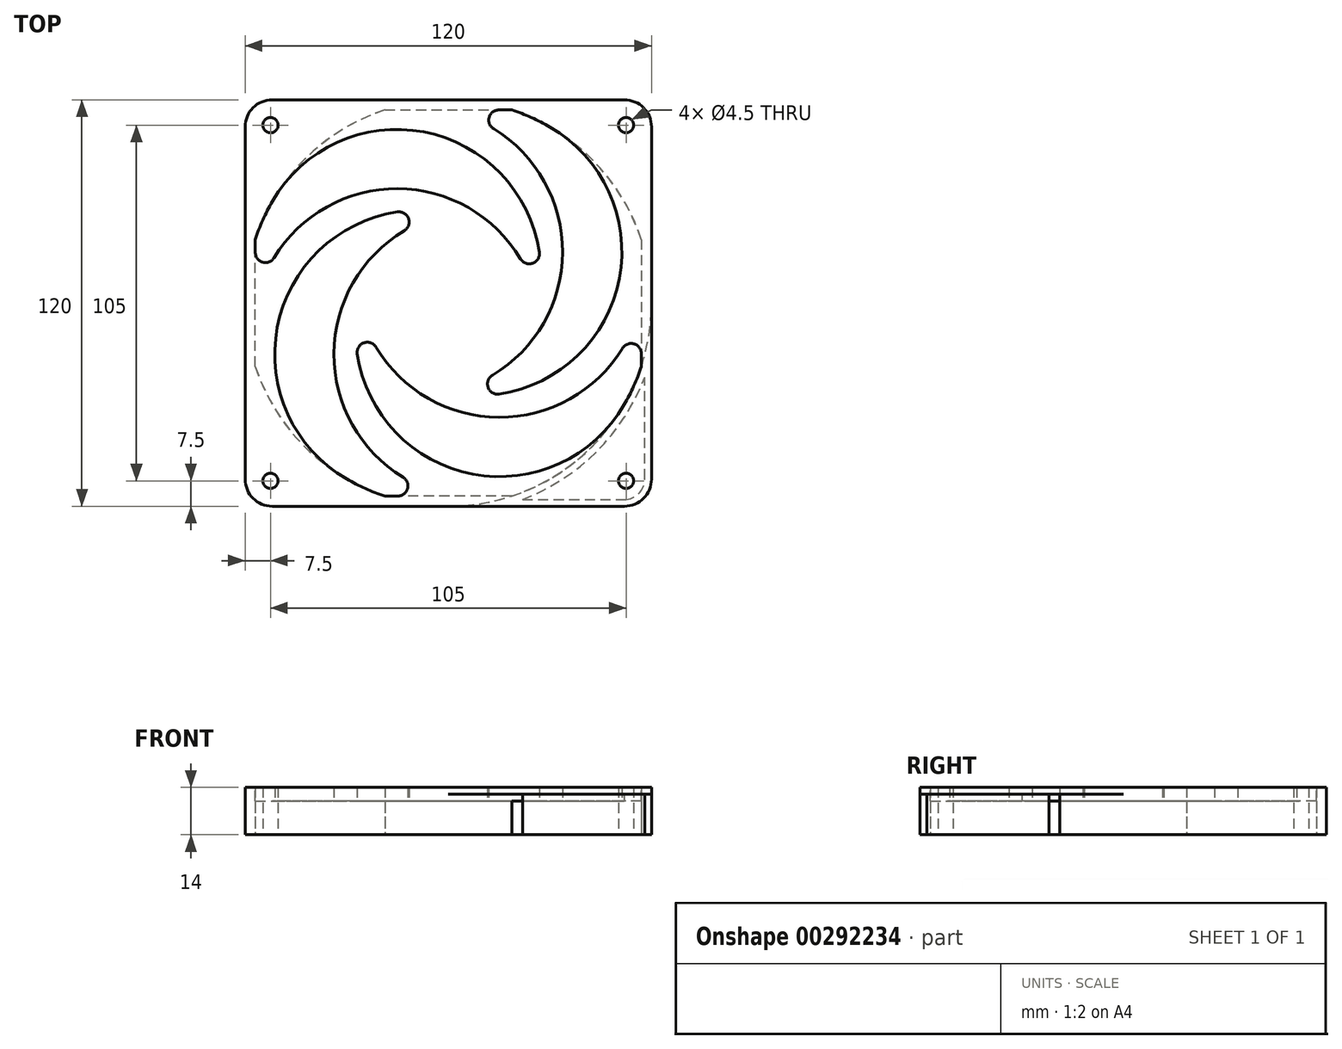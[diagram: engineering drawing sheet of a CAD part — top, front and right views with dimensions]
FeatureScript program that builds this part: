
annotation { "Feature Type Name" : "Feature", "Feature Type Description" : "" }
export const myFeature = defineFeature(function(context is Context, id is Id, definition is map)
    precondition{}
    {
        {
            var Q0;
            Q0=qCreatedBy(makeId("Top.planeOp"),FACE);
            var sketch = newSketch(context, id + "F0", { "sketchPlane" : qUnion([Q0])});
            skCircle(sketch, "E0", {"center": v(0, 0) * mm, "radius": 25 * mm});
            skLineSegment(sketch, "E1.bottom", {"start": v(52, 60) * mm, "end": v(-52, 60) * mm});
            skLineSegment(sketch, "E1.top", {"start": v(52, -60) * mm, "end": v(-52, -60) * mm});
            skLineSegment(sketch, "E1.left", {"start": v(60, 52) * mm, "end": v(60, -52) * mm});
            skLineSegment(sketch, "E1.right", {"start": v(-60, 52) * mm, "end": v(-60, -52) * mm});
            skCircle(sketch, "E2", {"center": v(0, 0) * mm, "radius": 60 * mm});
            skLineSegment(sketch, "E3.bottom", {"start": v(52.5, 52.5) * mm, "end": v(-52.5, 52.5) * mm, "construction": true});
            skLineSegment(sketch, "E3.top", {"start": v(52.5, -52.5) * mm, "end": v(-52.5, -52.5) * mm, "construction": true});
            skLineSegment(sketch, "E3.left", {"start": v(52.5, 52.5) * mm, "end": v(52.5, -52.5) * mm, "construction": true});
            skLineSegment(sketch, "E3.right", {"start": v(-52.5, 52.5) * mm, "end": v(-52.5, -52.5) * mm, "construction": true});
            skCircle(sketch, "E4", {"center": v(-52.5, 52.5) * mm, "radius": 2.25 * mm});
            skCircle(sketch, "E5", {"center": v(52.5, 52.5) * mm, "radius": 2.25 * mm});
            skCircle(sketch, "E6", {"center": v(52.5, -52.5) * mm, "radius": 2.25 * mm});
            skCircle(sketch, "E7", {"center": v(-52.5, -52.5) * mm, "radius": 2.25 * mm});
            skPoint(sketch, "E8.visualSharp", {"position": v(-60, 60) * mm});
            skArc(sketch, "E8.filletArc", {"start": v(-52, 60) * mm, "mid": v(-57.66, 57.66) * mm, "end": v(-60, 52) * mm});
            skPoint(sketch, "E9.visualSharp", {"position": v(60, 60) * mm});
            skArc(sketch, "E9.filletArc", {"start": v(60, 52) * mm, "mid": v(57.66, 57.66) * mm, "end": v(52, 60) * mm});
            skPoint(sketch, "E10.visualSharp", {"position": v(60, -60) * mm});
            skArc(sketch, "E10.filletArc", {"start": v(52, -60) * mm, "mid": v(57.66, -57.66) * mm, "end": v(60, -52) * mm});
            skPoint(sketch, "E11.visualSharp", {"position": v(-60, -60) * mm});
            skArc(sketch, "E11.filletArc", {"start": v(-60, -52) * mm, "mid": v(-57.66, -57.66) * mm, "end": v(-52, -60) * mm});
            skLineSegment(sketch, "E12", {"start": v(-18.73, 57) * mm, "end": v(18.73, 57) * mm});
            skLineSegment(sketch, "E13.1.0", {"start": v(-57, -18.73) * mm, "end": v(-57, 18.73) * mm});
            skLineSegment(sketch, "E13.2.0", {"start": v(18.73, -57) * mm, "end": v(-18.73, -57) * mm});
            skLineSegment(sketch, "E14.1.3.0", {"start": v(57, 18.73) * mm, "end": v(57, -18.73) * mm});
            skSolve(sketch);
        }
        {
            var Q0;
            Q0=makeQuery(id+"F0.imprint","IMPRINT",FACE,{"disambiguationData":[TD([[makeQuery(id+"F0.imprint","IMPRINT",EDGE,{"derivedFrom":sQuery(id+"F0.wireOp",EDGE,"E0")}),1.0]])]});
            var Q1;
            Q1=makeQuery(id+"F0.imprint","IMPRINT",FACE,{"disambiguationData":[TD([[makeQuery(id+"F0.imprint","IMPRINT",EDGE,{"derivedFrom":sQuery(id+"F0.wireOp",EDGE,"E0")}),-1.0]])]});
            var Q2;
            Q2=makeQuery(id+"F0.imprint","IMPRINT",FACE,{"disambiguationData":[TD([[makeQuery(id+"F0.imprint","IMPRINT",EDGE,{"derivedFrom":sQuery(id+"F0.wireOp",EDGE,"E4")}),-1.0]])]});
            var Q3;
            Q3=makeQuery(id+"F0.imprint","IMPRINT",FACE,{"disambiguationData":[TD([[makeQuery(id+"F0.imprint","IMPRINT",EDGE,{"derivedFrom":sQuery(id+"F0.wireOp",EDGE,"E7")}),-1.0]])]});
            var Q4;
            Q4=makeQuery(id+"F0.imprint","IMPRINT",FACE,{"disambiguationData":[TD([[makeQuery(id+"F0.imprint","IMPRINT",EDGE,{"derivedFrom":sQuery(id+"F0.wireOp",EDGE,"E6")}),-1.0]])]});
            var Q5;
            Q5=makeQuery(id+"F0.imprint","IMPRINT",FACE,{"disambiguationData":[TD([[makeQuery(id+"F0.imprint","IMPRINT",EDGE,{"derivedFrom":sQuery(id+"F0.wireOp",EDGE,"E5")}),-1.0]])]});
            var Q6;
            {var subQ0=sQuery(id+"F0.wireOp",EDGE,"E12");Q6=makeQuery(id+"F0.imprint","IMPRINT",FACE,{"disambiguationData":[TD([[makeQuery(id+"F0.imprint","IMPRINT",EDGE,{"derivedFrom":subQ0}),1.0]])]});}
            var Q7;
            {var subQ0=sQuery(id+"F0.wireOp",EDGE,"E13.1.0");Q7=makeQuery(id+"F0.imprint","IMPRINT",FACE,{"disambiguationData":[TD([[makeQuery(id+"F0.imprint","IMPRINT",EDGE,{"derivedFrom":subQ0}),1.0]])]});}
            var Q8;
            {var subQ0=sQuery(id+"F0.wireOp",EDGE,"E13.2.0");Q8=makeQuery(id+"F0.imprint","IMPRINT",FACE,{"disambiguationData":[TD([[makeQuery(id+"F0.imprint","IMPRINT",EDGE,{"derivedFrom":subQ0}),1.0]])]});}
            var Q9;
            {var subQ0=sQuery(id+"F0.wireOp",EDGE,"E14.1.3.0");Q9=makeQuery(id+"F0.imprint","IMPRINT",FACE,{"disambiguationData":[TD([[makeQuery(id+"F0.imprint","IMPRINT",EDGE,{"derivedFrom":subQ0}),1.0]])]});}
            extrude(context, id + "F1", {"entities" : qUnion([Q0, Q1, Q2, Q3, Q4, Q5, Q6, Q7, Q8, Q9]), "depth" : 14 * mm});
        }
        {
            var Q0;
            Q0=makeQuery(id+"F0.imprint","IMPRINT",FACE,{"disambiguationData":[TD([[makeQuery(id+"F0.imprint","IMPRINT",EDGE,{"derivedFrom":sQuery(id+"F0.wireOp",EDGE,"E0")}),-1.0]])]});
            var Q1;
            Q1=makeQuery(id+"F0.imprint","IMPRINT",FACE,{"disambiguationData":[TD([[makeQuery(id+"F0.imprint","IMPRINT",EDGE,{"derivedFrom":sQuery(id+"F0.wireOp",EDGE,"E0")}),1.0]])]});
            extrude(context, id + "F2", {"entities" : qUnion([Q0, Q1]), "operationType" : NewBodyOperationType.REMOVE, "depth" : 10 * mm});
        }
        {
            var Q0;
            Q0=makeQuery(id+"F0.imprint","IMPRINT",FACE,{"disambiguationData":[TD([[makeQuery(id+"F0.imprint","IMPRINT",EDGE,{"derivedFrom":sQuery(id+"F0.wireOp",EDGE,"E0")}),-1.0]])]});
            var sketch = newSketch(context, id + "F3", { "sketchPlane" : qUnion([Q0])});
            skLineSegment(sketch, "E15.0.0", {"start": v(57, -18.73) * mm, "end": v(57, 18.73) * mm});
            skArc(sketch, "E15.0.1", {"start": v(57, 18.73) * mm, "mid": v(42.43, 42.43) * mm, "end": v(18.73, 57) * mm});
            skLineSegment(sketch, "E15.0.2", {"start": v(18.73, 57) * mm, "end": v(-18.73, 57) * mm});
            skArc(sketch, "E15.0.3", {"start": v(-18.73, 57) * mm, "mid": v(-42.43, 42.43) * mm, "end": v(-57, 18.73) * mm});
            skLineSegment(sketch, "E15.0.4", {"start": v(-57, 18.73) * mm, "end": v(-57, -18.73) * mm});
            skArc(sketch, "E15.0.5", {"start": v(-57, -18.73) * mm, "mid": v(-42.43, -42.43) * mm, "end": v(-18.73, -57) * mm});
            skLineSegment(sketch, "E15.0.6", {"start": v(-18.73, -57) * mm, "end": v(18.73, -57) * mm});
            skArc(sketch, "E15.0.7", {"start": v(18.73, -57) * mm, "mid": v(42.43, -42.43) * mm, "end": v(57, -18.73) * mm});
            skCircle(sketch, "E16", {"center": v(0, 0) * mm, "radius": 25 * mm});
            skArc(sketch, "E17", {"start": v(12.5, 21.65) * mm, "mid": v(-45.56, 6.1) * mm, "end": v(-30, -51.96) * mm});
            skLineSegment(sketch, "E18", {"start": v(0, 0) * mm, "end": v(0, -16.93) * mm, "construction": true});
            skLineSegment(sketch, "E19", {"start": v(0, 0) * mm, "end": v(-8.75, -15.16) * mm, "construction": true});
            skArc(sketch, "E20", {"start": v(21.65, 12.5) * mm, "mid": v(-22.5, 33.1) * mm, "end": v(-57, -1.31) * mm});
            skLineSegment(sketch, "E21", {"start": v(0, 0) * mm, "end": v(-15.16, -8.75) * mm, "construction": true});
            skArc(sketch, "E22.1.0", {"start": v(-21.65, 12.5) * mm, "mid": v(-6.1, -45.56) * mm, "end": v(51.96, -30) * mm});
            skArc(sketch, "E22.1.1", {"start": v(-12.5, 21.65) * mm, "mid": v(-33.1, -22.5) * mm, "end": v(1.31, -57) * mm});
            skArc(sketch, "E22.2.0", {"start": v(-12.5, -21.65) * mm, "mid": v(45.56, -6.1) * mm, "end": v(30, 51.96) * mm});
            skArc(sketch, "E22.2.1", {"start": v(-21.65, -12.5) * mm, "mid": v(22.5, -33.1) * mm, "end": v(57, 1.31) * mm});
            skArc(sketch, "E23.3.3.0", {"start": v(21.65, -12.5) * mm, "mid": v(6.1, 45.56) * mm, "end": v(-51.96, 30) * mm});
            skArc(sketch, "E23.4.3.0", {"start": v(12.5, -21.65) * mm, "mid": v(33.1, 22.5) * mm, "end": v(-1.31, 57) * mm});
            skSolve(sketch);
        }
        {
            var Q0;
            {var subQ0=sQuery(id+"F3.wireOp",EDGE,"E22.1.0");Q0=makeQuery(id+"F3.imprint","IMPRINT",FACE,{"disambiguationData":[TD([[makeQuery(id+"F3.imprint","IMPRINT",EDGE,{"derivedFrom":subQ0}),1.0]])]});}
            var Q1;
            {var subQ0=sQuery(id+"F3.wireOp",EDGE,"E17");Q1=makeQuery(id+"F3.imprint","IMPRINT",FACE,{"disambiguationData":[TD([[makeQuery(id+"F3.imprint","IMPRINT",EDGE,{"derivedFrom":subQ0}),1.0]])]});}
            var Q2;
            {var subQ0=sQuery(id+"F3.wireOp",EDGE,"E22.2.0");Q2=makeQuery(id+"F3.imprint","IMPRINT",FACE,{"disambiguationData":[TD([[makeQuery(id+"F3.imprint","IMPRINT",EDGE,{"derivedFrom":subQ0}),1.0]])]});}
            var Q3;
            {var subQ0=sQuery(id+"F3.wireOp",EDGE,"E20");Q3=makeQuery(id+"F3.imprint","IMPRINT",FACE,{"disambiguationData":[TD([[makeQuery(id+"F3.imprint","IMPRINT",EDGE,{"derivedFrom":subQ0}),-1.0]])]});}
            extrude(context, id + "F4", {"entities" : qUnion([Q0, Q1, Q2, Q3]), "operationType" : NewBodyOperationType.REMOVE, "endBound" : BoundingType.THROUGH_ALL, "depth" : 25 * mm});
        }
        {
            var Q0;
            Q0=makeQuery(id+"F4.boolean.opBoolean","COPY",EDGE,{"derivedFrom":makeQuery(id+"F4.opExtrude","SWEPT_EDGE",EDGE,{"disambiguationData":[OSD([sQuery(id+"F3.wireOp",EDGE,"E16"),sQuery(id+"F3.wireOp",EDGE,"E23.3.3.0")])]})});
            var Q1;
            Q1=makeQuery(id+"F4.boolean.opBoolean","COPY",EDGE,{"derivedFrom":makeQuery(id+"F4.opExtrude","SWEPT_EDGE",EDGE,{"disambiguationData":[OSD([sQuery(id+"F3.wireOp",EDGE,"E16"),sQuery(id+"F3.wireOp",EDGE,"E17")])]})});
            var Q2;
            Q2=makeQuery(id+"F4.boolean.opBoolean","COPY",EDGE,{"derivedFrom":makeQuery(id+"F4.opExtrude","SWEPT_EDGE",EDGE,{"disambiguationData":[OSD([sQuery(id+"F3.wireOp",EDGE,"E16"),sQuery(id+"F3.wireOp",EDGE,"E22.1.0")])]})});
            var Q3;
            Q3=makeQuery(id+"F4.boolean.opBoolean","COPY",EDGE,{"derivedFrom":makeQuery(id+"F4.opExtrude","SWEPT_EDGE",EDGE,{"disambiguationData":[OSD([sQuery(id+"F3.wireOp",EDGE,"E16"),sQuery(id+"F3.wireOp",EDGE,"E22.2.0")])]})});
            var Q4;
            Q4=makeQuery(id+"F4.boolean.opBoolean","COPY",EDGE,{"derivedFrom":makeQuery(id+"F4.opExtrude","SWEPT_EDGE",EDGE,{"disambiguationData":[OSD([sQuery(id+"F3.wireOp",EDGE,"E15.0.4"),sQuery(id+"F3.wireOp",EDGE,"E20")])]})});
            var Q5;
            Q5=makeQuery(id+"F4.boolean.opBoolean","COPY",EDGE,{"derivedFrom":makeQuery(id+"F4.opExtrude","SWEPT_EDGE",EDGE,{"disambiguationData":[OSD([sQuery(id+"F3.wireOp",EDGE,"E15.0.2"),sQuery(id+"F3.wireOp",EDGE,"E23.4.3.0")])]})});
            var Q6;
            Q6=makeQuery(id+"F4.boolean.opBoolean","COPY",EDGE,{"derivedFrom":makeQuery(id+"F4.opExtrude","SWEPT_EDGE",EDGE,{"disambiguationData":[OSD([sQuery(id+"F3.wireOp",EDGE,"E15.0.0"),sQuery(id+"F3.wireOp",EDGE,"E22.2.1")])]})});
            var Q7;
            Q7=makeQuery(id+"F4.boolean.opBoolean","COPY",EDGE,{"derivedFrom":makeQuery(id+"F4.opExtrude","SWEPT_EDGE",EDGE,{"disambiguationData":[OSD([sQuery(id+"F3.wireOp",EDGE,"E15.0.6"),sQuery(id+"F3.wireOp",EDGE,"E22.1.1")])]})});
            fillet(context, id + "F5", {"entities" : qUnion([Q0, Q1, Q2, Q3, Q4, Q5, Q6, Q7]), "radius" : 3 * mm, "tangentPropagation" : true, "allowEdgeOverflow" : false});
        }
        {
            var Q0;
            Q0=makeQuery(id+"F0.imprint","IMPRINT",FACE,{"disambiguationData":[TD([[makeQuery(id+"F0.imprint","IMPRINT",EDGE,{"derivedFrom":sQuery(id+"F0.wireOp",EDGE,"E6")}),-1.0]])]});
            var sketch = newSketch(context, id + "F6", { "sketchPlane" : qUnion([Q0])});
            skLineSegment(sketch, "E24.0.0", {"start": v(0, -60) * mm, "end": v(52, -60) * mm});
            skArc(sketch, "E24.0.1", {"start": v(52, -60) * mm, "mid": v(57.66, -57.66) * mm, "end": v(60, -52) * mm});
            skLineSegment(sketch, "E24.0.2", {"start": v(60, -52) * mm, "end": v(60, 0) * mm});
            skArc(sketch, "E24.0.3", {"start": v(60, 0) * mm, "mid": v(59.25, -9.49) * mm, "end": v(57, -18.73) * mm});
            skArc(sketch, "E24.0.4", {"start": v(57, -18.73) * mm, "mid": v(42.43, -42.43) * mm, "end": v(18.73, -57) * mm});
            skArc(sketch, "E24.0.5", {"start": v(18.73, -57) * mm, "mid": v(9.49, -59.25) * mm, "end": v(0, -60) * mm});
            skCircle(sketch, "E25.0", {"center": v(52.5, -52.5) * mm, "radius": 2.25 * mm});
            skLineSegment(sketch, "E26.0", {"start": v(21.9, -58) * mm, "end": v(52, -58) * mm});
            skArc(sketch, "E26.1", {"start": v(58, -21.9) * mm, "mid": v(43.84, -43.84) * mm, "end": v(21.9, -58) * mm});
            skLineSegment(sketch, "E26.2", {"start": v(58, -52) * mm, "end": v(58, -21.9) * mm});
            skArc(sketch, "E26.3", {"start": v(52, -58) * mm, "mid": v(56.24, -56.24) * mm, "end": v(58, -52) * mm});
            skCircle(sketch, "E27", {"center": v(52.5, -52.5) * mm, "radius": 5.3 * mm});
            skArc(sketch, "E28", {"start": v(48.1, -58) * mm, "mid": v(49.03, -57.38) * mm, "end": v(48.8, -56.28) * mm});
            skArc(sketch, "E29", {"start": v(56.28, -48.8) * mm, "mid": v(57.38, -49.03) * mm, "end": v(58, -48.1) * mm});
            skSolve(sketch);
        }
        {
            var Q0;
            {var subQ1=sQuery(id+"F6.wireOp",EDGE,"E26.1");Q0=makeQuery(id+"F6.imprint","IMPRINT",FACE,{"disambiguationData":[TD([[makeQuery(id+"F6.imprint","IMPRINT",EDGE,{"derivedFrom":subQ1}),1.0]])]});}
            var Q1;
            Q1=makeQuery(id+"F2.boolean.opBoolean","COPY",FACE,{"derivedFrom":makeQuery(id+"F2.opExtrude","CAP_FACE",FACE,{"disambiguationData":[OSD([sQuery(id+"F0.wireOp",EDGE,"E2"),sQuery(id+"F0.wireOp",EDGE,"E12"),sQuery(id+"F0.wireOp",EDGE,"E13.1.0"),sQuery(id+"F0.wireOp",EDGE,"E13.2.0"),sQuery(id+"F0.wireOp",EDGE,"E14.1.3.0")])],"isStart":false})});
            extrude(context, id + "F7", {"entities" : qUnion([Q0]), "operationType" : NewBodyOperationType.REMOVE, "endBoundEntityFace" : qUnion([Q1]), "depth" : 12 * mm});
        }
    });
